# Revit family: VENTS-QUIETLINE
name_source: partatom
category: Mechanical Equipment
units: mm (PartAtom-declared; Revit-internal decimal feet)

## family parameters
Always vertical = Yes
Classification = None
Cut with Voids When Loaded = No
OmniClass Number = 23.75.35.17.11
OmniClass Title = Fans for Air Ductwork
Part Type = Breaks Into
Room Calculation Point = No
Round Connector Dimension = Use Diameter
Shared = No
Work Plane-Based = No

## types (3) — shared parameters
Casing Material = Plastic White Glazed
Current = 0 A
Description = Inline axial fan for round ducts
Family Version = 1.0
Load Classification = HVAC
Maintenance Zone Height = 600 mm
Maintenance Zone Length = 400 mm  [stored 1.31234 ft]
Maintenance Zone Material = Maintenance Zone
Maintenance Zone Width = 400 mm  [stored 1.31234 ft]
Manufacturer = Vents
Model = Quietline 100
Number of Poles = 1
Power Factor = 1
Protection rating = IPX4
Transported Air Temperature (°C) = +1...+40
Type Comments = Inline axial fan Quietline 100
URL = https://ventilation-system.com
Voltage = 230 V
dFl = 23 mm  [stored 0.0754593 ft]
sFl = 2 mm  [stored 0.00656168 ft]

## per-type parameters (varying)
| type | Apparent Power | Connection Diameter | D | L | Maximum Air Flow | Noise Level at 3 m (dBa) | Power | RPM (min-1) | Weight | gsD |
| Quietline 100 | 8 VA | 100 mm  [stored 0.328084 ft] | 100 mm  [stored 0.328084 ft] | 138 mm  [stored 0.452756 ft] | 100 m³/h | 25 | 8 W | 2100 | 0.61 kg | 110 mm |
| Quietline 125 | 13 VA | 125 mm  [stored 0.410105 ft] | 125 mm  [stored 0.410105 ft] | 162 mm  [stored 0.531496 ft] | 197 m³/h | 32 | 13 W | 2250 | 0.75 kg | 130 mm |
| Quietline 150 | 22 VA | 150 mm | 150 mm | 182 mm  [stored 0.597113 ft] | 335 m³/h | 37 | 22 W | 2250 | 1.30 kg | 146 mm |

note: [stored X ft] marks values corroborated as IEEE doubles in the binary element streams (Revit-internal decimal feet)

## geometry (parser evidence)
native form markers: Sweep x7
no freeform markers — native parametric forms only
